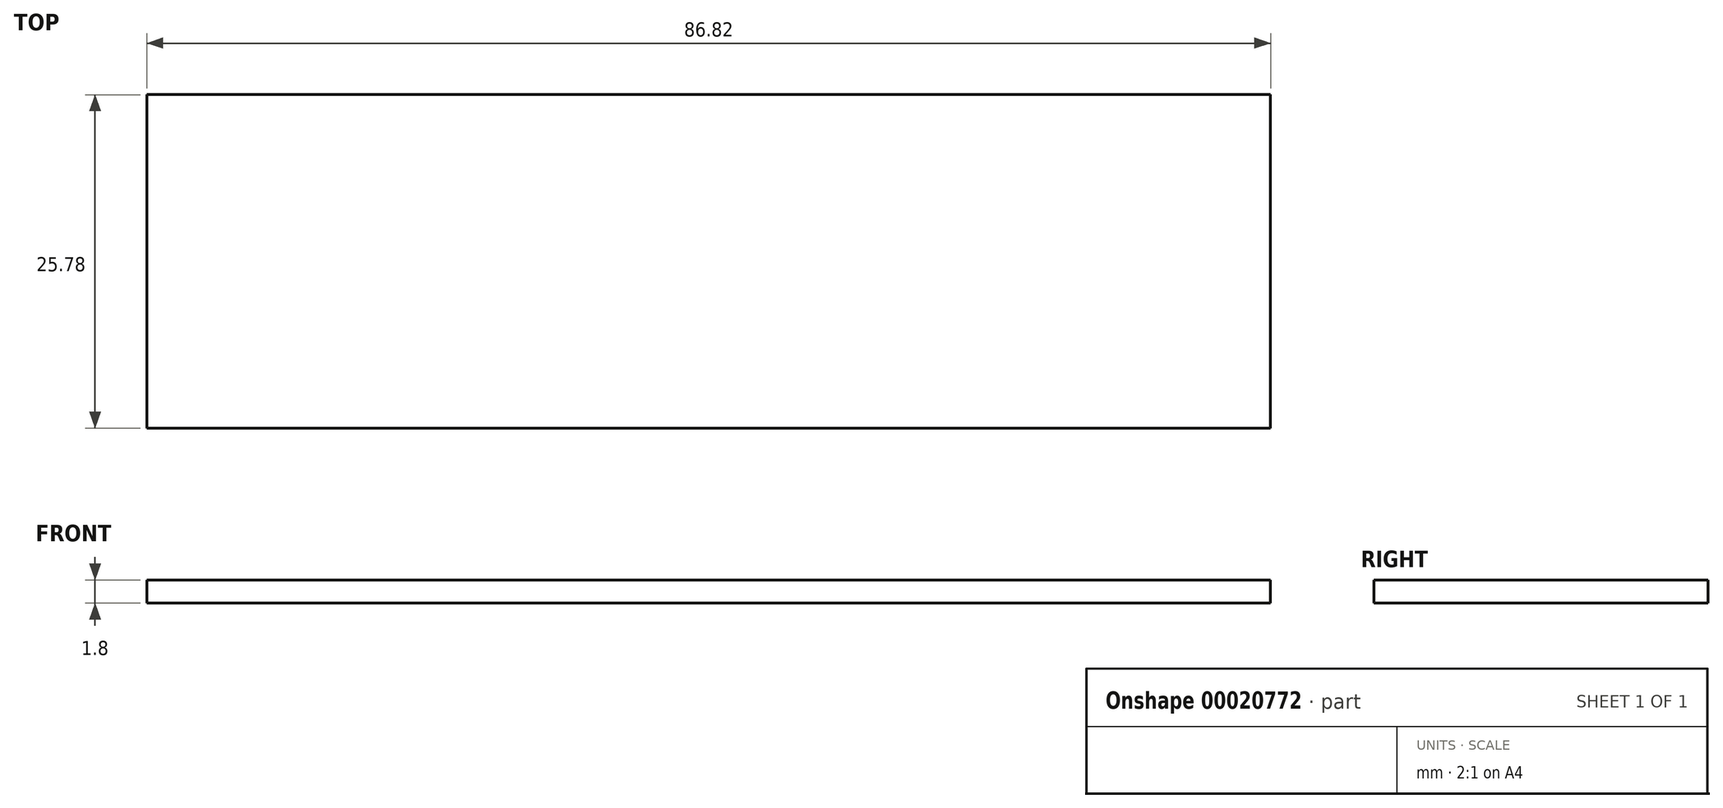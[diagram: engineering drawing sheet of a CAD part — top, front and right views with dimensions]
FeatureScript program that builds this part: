
annotation { "Feature Type Name" : "Feature", "Feature Type Description" : "" }
export const myFeature = defineFeature(function(context is Context, id is Id, definition is map)
    precondition{}
    {
        {
            var Q0;
            Q0=qCreatedBy(makeId("Top.planeOp"),FACE);
            var sketch = newSketch(context, id + "F0", { "sketchPlane" : qUnion([Q0])});
            skLineSegment(sketch, "E0.bottom", {"start": v(-39.14, 20.31) * mm, "end": v(47.68, 20.31) * mm});
            skLineSegment(sketch, "E0.top", {"start": v(-39.14, -5.47) * mm, "end": v(47.68, -5.47) * mm});
            skLineSegment(sketch, "E0.left", {"start": v(-39.14, 20.31) * mm, "end": v(-39.14, -5.47) * mm});
            skLineSegment(sketch, "E0.right", {"start": v(47.68, 20.31) * mm, "end": v(47.68, -5.47) * mm});
            skSolve(sketch);
        }
        {
            var Q0;
            Q0 = qSketchRegion(id + "F0", true);
            extrude(context, id + "F1", {"entities" : qUnion([Q0]), "depth" : 1.8 * mm});
        }
    });
